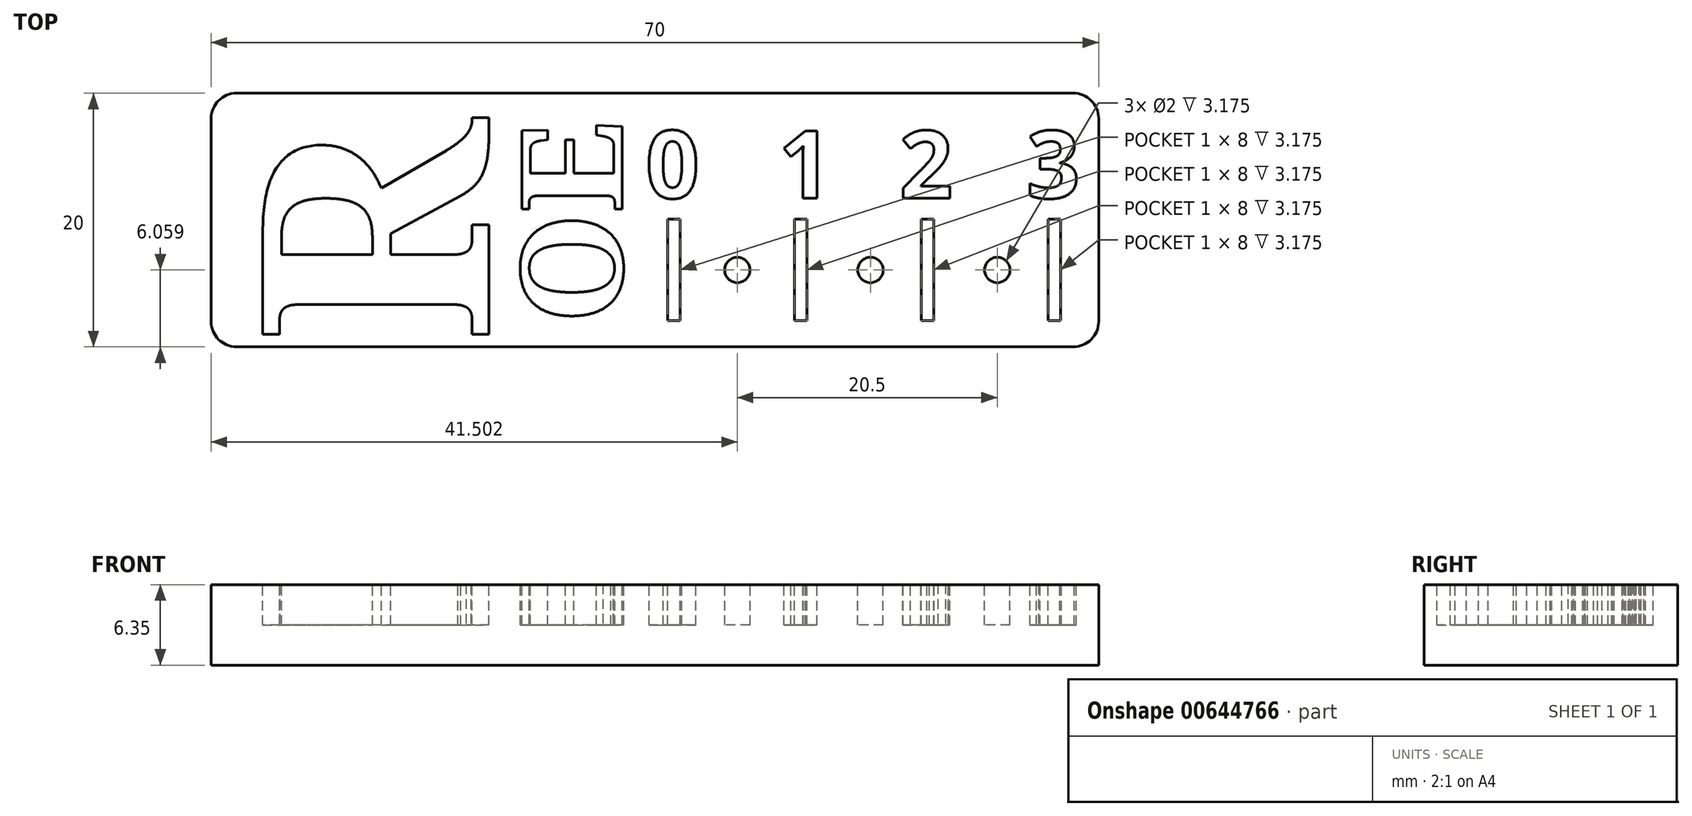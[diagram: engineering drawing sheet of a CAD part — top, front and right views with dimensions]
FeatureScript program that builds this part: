
annotation { "Feature Type Name" : "Feature", "Feature Type Description" : "" }
export const myFeature = defineFeature(function(context is Context, id is Id, definition is map)
    precondition{}
    {
        {
            var Q0;
            Q0=qCreatedBy(makeId("Top.planeOp"),FACE);
            var sketch = newSketch(context, id + "F0", { "sketchPlane" : qUnion([Q0])});
            skLineSegment(sketch, "E0.bottom", {"start": v(-55.27, 9.73) * mm, "end": v(10.73, 9.73) * mm});
            skLineSegment(sketch, "E0.top", {"start": v(-55.27, -10.27) * mm, "end": v(10.73, -10.27) * mm});
            skLineSegment(sketch, "E0.left", {"start": v(-57.27, 7.73) * mm, "end": v(-57.27, -8.27) * mm});
            skLineSegment(sketch, "E0.right", {"start": v(12.73, 7.73) * mm, "end": v(12.73, -8.27) * mm});
            skPoint(sketch, "E1.visualSharp", {"position": v(-57.27, 9.73) * mm});
            skArc(sketch, "E1.filletArc", {"start": v(-55.27, 9.73) * mm, "mid": v(-56.68, 9.15) * mm, "end": v(-57.27, 7.73) * mm});
            skPoint(sketch, "E2.visualSharp", {"position": v(12.73, 9.73) * mm});
            skArc(sketch, "E2.filletArc", {"start": v(12.73, 7.73) * mm, "mid": v(12.14, 9.15) * mm, "end": v(10.73, 9.73) * mm});
            skPoint(sketch, "E3.visualSharp", {"position": v(12.73, -10.27) * mm});
            skArc(sketch, "E3.filletArc", {"start": v(10.73, -10.27) * mm, "mid": v(12.14, -9.68) * mm, "end": v(12.73, -8.27) * mm});
            skPoint(sketch, "E4.visualSharp", {"position": v(-57.27, -10.27) * mm});
            skArc(sketch, "E4.filletArc", {"start": v(-57.27, -8.27) * mm, "mid": v(-56.68, -9.68) * mm, "end": v(-55.27, -10.27) * mm});
            skSolve(sketch);
        }
        {
            var Q0;
            Q0=qSketchRegion(id+"F0",true);
            extrude(context, id + "F1", {"entities" : qUnion([Q0]), "depth" : 6.35 * mm, "offsetDistance" : 25.4 * mm});
        }
        {
            var Q0;
            Q0=makeQuery(id+"F1.opExtrude","CAP_FACE",FACE,{"disambiguationData":[OSD([sQuery(id+"F0.wireOp",EDGE,"E0.bottom"),sQuery(id+"F0.wireOp",EDGE,"E0.top"),sQuery(id+"F0.wireOp",EDGE,"E0.left"),sQuery(id+"F0.wireOp",EDGE,"E0.right")])],"isStart":false});
            var sketch = newSketch(context, id + "F2", { "sketchPlane" : qUnion([Q0])});
            skText(sketch, "E5", { "text": "R", "fontName": "NotoSerif-Bold.ttf"});
            skText(sketch, "E6", { "text": "OE", "fontName": "NotoSerif-Bold.ttf"});
            skLineSegment(sketch, "E7.bottom", {"start": v(-21.27, -0.21) * mm, "end": v(-20.27, -0.21) * mm});
            skLineSegment(sketch, "E7.top", {"start": v(-21.27, -8.21) * mm, "end": v(-20.27, -8.21) * mm});
            skLineSegment(sketch, "E7.left", {"start": v(-21.27, -0.21) * mm, "end": v(-21.27, -8.21) * mm});
            skLineSegment(sketch, "E7.right", {"start": v(-20.27, -0.21) * mm, "end": v(-20.27, -8.21) * mm});
            skLineSegment(sketch, "E8.bottom", {"start": v(-11.27, -0.21) * mm, "end": v(-10.27, -0.21) * mm});
            skLineSegment(sketch, "E8.top", {"start": v(-11.27, -8.21) * mm, "end": v(-10.27, -8.21) * mm});
            skLineSegment(sketch, "E8.left", {"start": v(-11.27, -0.21) * mm, "end": v(-11.27, -8.21) * mm});
            skLineSegment(sketch, "E8.right", {"start": v(-10.27, -0.21) * mm, "end": v(-10.27, -8.21) * mm});
            skLineSegment(sketch, "E9.bottom", {"start": v(-1.27, -0.21) * mm, "end": v(-0.27, -0.21) * mm});
            skLineSegment(sketch, "E9.top", {"start": v(-1.27, -8.21) * mm, "end": v(-0.27, -8.21) * mm});
            skLineSegment(sketch, "E9.left", {"start": v(-1.27, -0.21) * mm, "end": v(-1.27, -8.21) * mm});
            skLineSegment(sketch, "E9.right", {"start": v(-0.27, -0.21) * mm, "end": v(-0.27, -8.21) * mm});
            skLineSegment(sketch, "E10.bottom", {"start": v(8.73, -0.21) * mm, "end": v(9.73, -0.21) * mm});
            skLineSegment(sketch, "E10.top", {"start": v(8.73, -8.21) * mm, "end": v(9.73, -8.21) * mm});
            skLineSegment(sketch, "E10.left", {"start": v(8.73, -0.21) * mm, "end": v(8.73, -8.21) * mm});
            skLineSegment(sketch, "E10.right", {"start": v(9.73, -0.21) * mm, "end": v(9.73, -8.21) * mm});
            skPoint(sketch, "E11", {"position": v(-20.77, -0.21) * mm});
            skPoint(sketch, "E12", {"position": v(-10.77, -0.21) * mm});
            skPoint(sketch, "E13", {"position": v(-0.77, -0.21) * mm});
            skCircle(sketch, "E14", {"center": v(-15.77, -4.21) * mm, "radius": 1 * mm});
            skPoint(sketch, "E15", {"position": v(-20.27, -4.21) * mm});
            skCircle(sketch, "E16", {"center": v(-5.27, -4.21) * mm, "radius": 1 * mm});
            skCircle(sketch, "E17", {"center": v(4.73, -4.21) * mm, "radius": 1 * mm});
            skPoint(sketch, "E18", {"position": v(-10.27, -4.21) * mm});
            skPoint(sketch, "E19", {"position": v(-0.27, -4.21) * mm});
            skText(sketch, "E20", { "text": "0", "fontName": "OpenSans-Bold.ttf"});
            skText(sketch, "E21", { "text": "1", "fontName": "OpenSans-Bold.ttf"});
            skText(sketch, "E22", { "text": "2", "fontName": "OpenSans-Bold.ttf"});
            skText(sketch, "E23", { "text": "3", "fontName": "OpenSans-Bold.ttf"});
            skPoint(sketch, "E24", {"position": v(-57.27, -0.27) * mm});
            const initialGuessF2  = {"E5": [-0.03535, -0.00996, 0, 1, 0.018], "E6": [-0.02484, -0.00845, 0, 1, 0.008], "E20": [-0.023, 0.00146, 1, 0, 0.00534], "E21": [-0.01254, 0.00146, 1, 0, 0.00534], "E22": [-0.003, 0.00146, 1, 0, 0.00534], "E23": [0.00702, 0.00146, 1, 0, 0.00534]};
            skSetInitialGuess(sketch, initialGuessF2);
            skSolve(sketch);
        }
        {
            var Q0;
            Q0=qSketchRegion(id+"F2",true);
            extrude(context, id + "F3", {"entities" : qUnion([Q0]), "operationType" : NewBodyOperationType.REMOVE, "oppositeDirection" : true, "depth" : 3.17 * mm, "offsetDistance" : 25.4 * mm});
        }
    });
